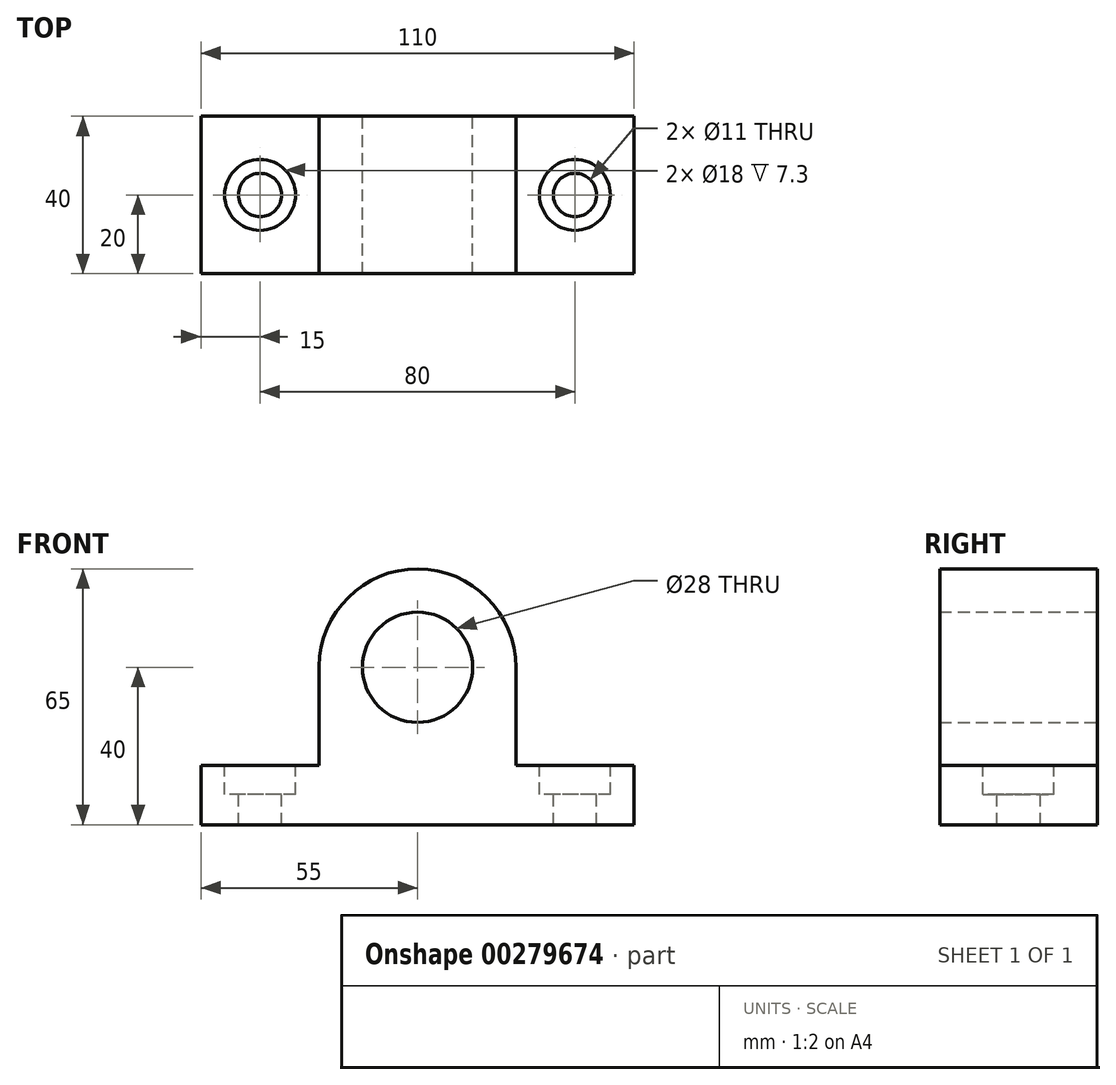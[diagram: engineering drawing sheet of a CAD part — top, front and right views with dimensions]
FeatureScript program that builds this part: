
annotation { "Feature Type Name" : "Feature", "Feature Type Description" : "" }
export const myFeature = defineFeature(function(context is Context, id is Id, definition is map)
    precondition{}
    {
        {
            var Q0;
            Q0=qCreatedBy(makeId("Front.planeOp"),FACE);
            var sketch = newSketch(context, id + "F0", { "sketchPlane" : qUnion([Q0])});
            skLineSegment(sketch, "E0", {"start": v(-55, -19) * mm, "end": v(-55, -34) * mm});
            skLineSegment(sketch, "E1", {"start": v(-55, -34) * mm, "end": v(55, -34) * mm});
            skLineSegment(sketch, "E2", {"start": v(55, -34) * mm, "end": v(55, -19) * mm});
            skLineSegment(sketch, "E3", {"start": v(55, -19) * mm, "end": v(25, -19) * mm});
            skLineSegment(sketch, "E4", {"start": v(25, -19) * mm, "end": v(25, 6) * mm});
            skLineSegment(sketch, "E5", {"start": v(-55, -19) * mm, "end": v(-25, -19) * mm});
            skLineSegment(sketch, "E6", {"start": v(-25, -19) * mm, "end": v(-25, 6.18) * mm});
            skArc(sketch, "E7", {"start": v(25, 6) * mm, "mid": v(0.1, 31) * mm, "end": v(-25, 6.18) * mm});
            skCircle(sketch, "E8", {"center": v(0, 6) * mm, "radius": 14 * mm});
            skSolve(sketch);
        }
        {
            var Q0;
            Q0 = qSketchRegion(id + "F0", true);
            extrude(context, id + "F1", {"entities" : qUnion([Q0]), "endBound" : BoundingType.SYMMETRIC, "depth" : 40 * mm});
        }
        {
            var Q0;
            Q0=makeQuery(id+"F1.opExtrude","SWEPT_FACE",FACE,{"disambiguationData":[OSD([sQuery(id+"F0.wireOp",EDGE,"E5")])]});
            var sketch = newSketch(context, id + "F2", { "sketchPlane" : qUnion([Q0])});
            skCircle(sketch, "E9", {"center": v(-40, 0) * mm, "radius": 9 * mm});
            skCircle(sketch, "E10", {"center": v(-40, 0) * mm, "radius": 5.5 * mm});
            skPoint(sketch, "E11.center.orphan", {"position": v(40.98, 0) * mm});
            skSolve(sketch);
        }
        {
            var Q0;
            Q0=makeQuery(id+"F2.imprint","IMPRINT",FACE,{"disambiguationData":[TD([[makeQuery(id+"F2.imprint","IMPRINT",EDGE,{"derivedFrom":sQuery(id+"F2.wireOp",EDGE,"E10")}),1.0]])]});
            extrude(context, id + "F3", {"entities" : qUnion([Q0]), "operationType" : NewBodyOperationType.REMOVE, "oppositeDirection" : true, "depth" : 15 * mm});
        }
        {
            var Q0;
            Q0 = qSketchRegion(id + "F2", true);
            extrude(context, id + "F4", {"entities" : qUnion([Q0]), "operationType" : NewBodyOperationType.REMOVE, "oppositeDirection" : true, "depth" : 7.3 * mm});
        }
        {
            var Q0;
            Q0=makeQuery(id+"F1.opExtrude","SWEPT_FACE",FACE,{"disambiguationData":[OSD([sQuery(id+"F0.wireOp",EDGE,"E3")])]});
            var sketch = newSketch(context, id + "F5", { "sketchPlane" : qUnion([Q0])});
            skCircle(sketch, "E12", {"center": v(40, 0) * mm, "radius": 9 * mm});
            skCircle(sketch, "E13", {"center": v(40, 0) * mm, "radius": 5.5 * mm});
            skSolve(sketch);
        }
        {
            var Q0;
            Q0=makeQuery(id+"F5.imprint","IMPRINT",FACE,{"disambiguationData":[TD([[makeQuery(id+"F5.imprint","IMPRINT",EDGE,{"derivedFrom":sQuery(id+"F5.wireOp",EDGE,"E13")}),1.0]])]});
            extrude(context, id + "F6", {"entities" : qUnion([Q0]), "operationType" : NewBodyOperationType.REMOVE, "oppositeDirection" : true, "depth" : 15 * mm});
        }
        {
            var Q0;
            Q0 = qSketchRegion(id + "F5", true);
            extrude(context, id + "F7", {"entities" : qUnion([Q0]), "operationType" : NewBodyOperationType.REMOVE, "oppositeDirection" : true, "depth" : 7.3 * mm});
        }
    });
